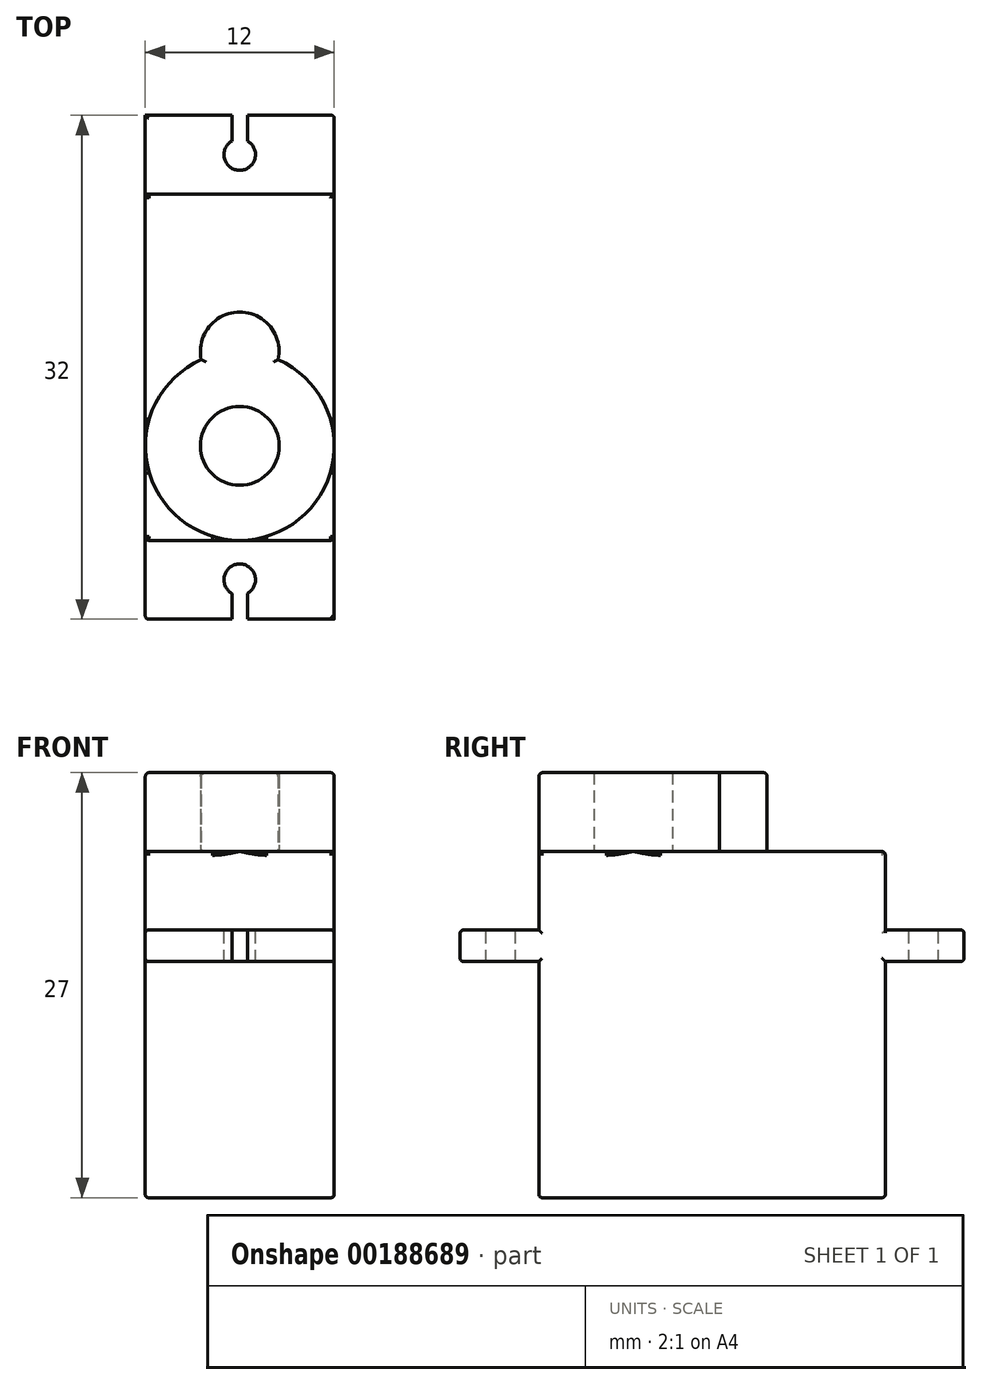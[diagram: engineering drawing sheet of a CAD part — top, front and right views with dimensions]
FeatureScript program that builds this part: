
annotation { "Feature Type Name" : "Feature", "Feature Type Description" : "" }
export const myFeature = defineFeature(function(context is Context, id is Id, definition is map)
    precondition{}
    {
        {
            var Q0;
            Q0=qCreatedBy(makeId("Top.planeOp"),FACE);
            var sketch = newSketch(context, id + "F0", { "sketchPlane" : qUnion([Q0])});
            skLineSegment(sketch, "E0.bottom", {"start": v(-8.25, -0.4) * mm, "end": v(3.75, -0.4) * mm});
            skLineSegment(sketch, "E0.top", {"start": v(-8.25, -22.4) * mm, "end": v(3.75, -22.4) * mm});
            skLineSegment(sketch, "E0.left", {"start": v(-8.25, -0.4) * mm, "end": v(-8.25, -22.4) * mm});
            skLineSegment(sketch, "E0.right", {"start": v(3.75, -0.4) * mm, "end": v(3.75, -22.4) * mm});
            skSolve(sketch);
        }
        {
            var Q0;
            Q0=makeQuery(id+"F0.imprint","IMPRINT",FACE,{"disambiguationData":[TD([[makeQuery(id+"F0.imprint","IMPRINT",EDGE,{"derivedFrom":sQuery(id+"F0.wireOp",EDGE,"E0.bottom")}),-1.0]])]});
            extrude(context, id + "F1", {"entities" : qUnion([Q0]), "depth" : 22 * mm});
        }
        {
            var Q0;
            Q0=makeQuery(id+"F1.opExtrude","CAP_FACE",FACE,{"disambiguationData":[OSD([sQuery(id+"F0.wireOp",EDGE,"E0.bottom"),sQuery(id+"F0.wireOp",EDGE,"E0.top"),sQuery(id+"F0.wireOp",EDGE,"E0.left"),sQuery(id+"F0.wireOp",EDGE,"E0.right")])],"isStart":false});
            var sketch = newSketch(context, id + "F2", { "sketchPlane" : qUnion([Q0])});
            skCircle(sketch, "E1", {"center": v(-2.25, -16.4) * mm, "radius": 6 * mm});
            skCircle(sketch, "E2", {"center": v(-2.25, -16.4) * mm, "radius": 2.5 * mm});
            skCircle(sketch, "E3", {"center": v(-2.25, -10.4) * mm, "radius": 2.5 * mm});
            skSolve(sketch);
        }
        {
            var Q0;
            {var subQ0=sQuery(id+"F2.wireOp",EDGE,"E3");var subQ1=sQuery(id+"F2.wireOp",EDGE,"E1");var subQ3=makeQuery(id+"F2.imprint","INTERSECT",VERTEX,{"disambiguationData":[OD(0.0)],"derivedFrom":[subQ1,subQ0]});Q0=makeQuery(id+"F2.imprint","IMPRINT",FACE,{"disambiguationData":[TD([[makeQuery(id+"F2.imprint","IMPRINT",EDGE,{"disambiguationData":[TD([[subQ3,-1.0]])],"derivedFrom":subQ1}),-1.0]])]});}
            var Q1;
            {var subQ0=sQuery(id+"F2.wireOp",EDGE,"E3");var subQ1=sQuery(id+"F2.wireOp",EDGE,"E1");var subQ3=makeQuery(id+"F2.imprint","INTERSECT",VERTEX,{"disambiguationData":[OD(0.0)],"derivedFrom":[subQ1,subQ0]});Q1=makeQuery(id+"F2.imprint","IMPRINT",FACE,{"disambiguationData":[TD([[makeQuery(id+"F2.imprint","IMPRINT",EDGE,{"disambiguationData":[TD([[subQ3,-1.0]])],"derivedFrom":subQ1}),1.0]])]});}
            var Q2;
            Q2=makeQuery(id+"F2.imprint","IMPRINT",FACE,{"disambiguationData":[TD([[makeQuery(id+"F2.imprint","IMPRINT",EDGE,{"derivedFrom":sQuery(id+"F2.wireOp",EDGE,"E2")}),-1.0]])]});
            extrude(context, id + "F3", {"entities" : qUnion([Q0, Q1, Q2]), "operationType" : NewBodyOperationType.ADD, "depth" : 5 * mm});
        }
        {
            var Q0;
            Q0=makeQuery(id+"F3.opExtrude","CAP_EDGE",EDGE,{"disambiguationData":[OSD([sQuery(id+"F2.wireOp",EDGE,"E1")])],"isStart":false});
            var Q1;
            Q1=makeQuery(id+"F3.opExtrude","CAP_EDGE",EDGE,{"disambiguationData":[OSD([sQuery(id+"F2.wireOp",EDGE,"E3")])],"isStart":false});
            var Q2;
            {var subQ0=sQuery(id+"F0.wireOp",EDGE,"E0.right");var subQ1=sQuery(id+"F0.wireOp",EDGE,"E0.bottom");Q2=makeQuery(id+"F3.boolean.opBoolean","SPLIT",EDGE,{"disambiguationData":[TD([makeQuery(id+"F1.opExtrude","SWEPT_FACE",FACE,{"disambiguationData":[OSD([subQ1])]})])],"derivedFrom":makeQuery(id+"F1.opExtrude","CAP_EDGE",EDGE,{"disambiguationData":[OSD([subQ0])],"isStart":false})});}
            var Q3;
            Q3=makeQuery(id+"F1.opExtrude","CAP_EDGE",EDGE,{"disambiguationData":[OSD([sQuery(id+"F0.wireOp",EDGE,"E0.bottom")])],"isStart":false});
            var Q4;
            {var subQ0=sQuery(id+"F0.wireOp",EDGE,"E0.left");var subQ1=sQuery(id+"F0.wireOp",EDGE,"E0.bottom");Q4=makeQuery(id+"F3.boolean.opBoolean","SPLIT",EDGE,{"disambiguationData":[TD([makeQuery(id+"F1.opExtrude","SWEPT_FACE",FACE,{"disambiguationData":[OSD([subQ1])]})])],"derivedFrom":makeQuery(id+"F1.opExtrude","CAP_EDGE",EDGE,{"disambiguationData":[OSD([subQ0])],"isStart":false})});}
            var Q5;
            {var subQ0=sQuery(id+"F0.wireOp",EDGE,"E0.right");var subQ1=sQuery(id+"F0.wireOp",EDGE,"E0.top");Q5=makeQuery(id+"F3.boolean.opBoolean","SPLIT",EDGE,{"disambiguationData":[TD([makeQuery(id+"F1.opExtrude","SWEPT_FACE",FACE,{"disambiguationData":[OSD([subQ1])]})])],"derivedFrom":makeQuery(id+"F1.opExtrude","CAP_EDGE",EDGE,{"disambiguationData":[OSD([subQ0])],"isStart":false})});}
            var Q6;
            {var subQ0=sQuery(id+"F0.wireOp",EDGE,"E0.top");var subQ1=sQuery(id+"F0.wireOp",EDGE,"E0.right");Q6=makeQuery(id+"F3.boolean.opBoolean","SPLIT",EDGE,{"disambiguationData":[TD([makeQuery(id+"F1.opExtrude","SWEPT_FACE",FACE,{"disambiguationData":[OSD([subQ1])]})])],"derivedFrom":makeQuery(id+"F1.opExtrude","CAP_EDGE",EDGE,{"disambiguationData":[OSD([subQ0])],"isStart":false})});}
            var Q7;
            {var subQ0=sQuery(id+"F0.wireOp",EDGE,"E0.top");var subQ1=sQuery(id+"F0.wireOp",EDGE,"E0.left");Q7=makeQuery(id+"F3.boolean.opBoolean","SPLIT",EDGE,{"disambiguationData":[TD([makeQuery(id+"F1.opExtrude","SWEPT_FACE",FACE,{"disambiguationData":[OSD([subQ1])]})])],"derivedFrom":makeQuery(id+"F1.opExtrude","CAP_EDGE",EDGE,{"disambiguationData":[OSD([subQ0])],"isStart":false})});}
            var Q8;
            {var subQ0=sQuery(id+"F0.wireOp",EDGE,"E0.left");var subQ1=sQuery(id+"F0.wireOp",EDGE,"E0.top");Q8=makeQuery(id+"F3.boolean.opBoolean","SPLIT",EDGE,{"disambiguationData":[TD([makeQuery(id+"F1.opExtrude","SWEPT_FACE",FACE,{"disambiguationData":[OSD([subQ1])]})])],"derivedFrom":makeQuery(id+"F1.opExtrude","CAP_EDGE",EDGE,{"disambiguationData":[OSD([subQ0])],"isStart":false})});}
            fillet(context, id + "F4", {"entities" : qUnion([Q0, Q1, Q2, Q3, Q4, Q5, Q6, Q7, Q8]), "radius" : .25 * mm, "tangentPropagation" : true, "allowEdgeOverflow" : false});
        }
        {
            var Q0;
            Q0=makeQuery(id+"F1.opExtrude","SWEPT_FACE",FACE,{"disambiguationData":[OSD([sQuery(id+"F0.wireOp",EDGE,"E0.bottom")])]});
            var sketch = newSketch(context, id + "F5", { "sketchPlane" : qUnion([Q0])});
            skLineSegment(sketch, "E4.bottom", {"start": v(-3.75, 17) * mm, "end": v(8.25, 17) * mm});
            skLineSegment(sketch, "E4.top", {"start": v(-3.75, 15) * mm, "end": v(8.25, 15) * mm});
            skLineSegment(sketch, "E4.left", {"start": v(-3.75, 17) * mm, "end": v(-3.75, 15) * mm});
            skLineSegment(sketch, "E4.right", {"start": v(8.25, 17) * mm, "end": v(8.25, 15) * mm});
            skSolve(sketch);
        }
        {
            var Q0;
            Q0=makeQuery(id+"F1.opExtrude","SWEPT_FACE",FACE,{"disambiguationData":[OSD([sQuery(id+"F0.wireOp",EDGE,"E0.top")])]});
            var sketch = newSketch(context, id + "F6", { "sketchPlane" : qUnion([Q0])});
            skLineSegment(sketch, "E5.bottom", {"start": v(-8.25, 17) * mm, "end": v(3.75, 17) * mm});
            skLineSegment(sketch, "E5.top", {"start": v(-8.25, 15) * mm, "end": v(3.75, 15) * mm});
            skLineSegment(sketch, "E5.left", {"start": v(-8.25, 17) * mm, "end": v(-8.25, 15) * mm});
            skLineSegment(sketch, "E5.right", {"start": v(3.75, 17) * mm, "end": v(3.75, 15) * mm});
            skSolve(sketch);
        }
        {
            var Q0;
            Q0=makeQuery(id+"F6.imprint","IMPRINT",FACE,{"disambiguationData":[TD([[makeQuery(id+"F6.imprint","IMPRINT",EDGE,{"derivedFrom":sQuery(id+"F6.wireOp",EDGE,"E5.bottom")}),-1.0]])]});
            extrude(context, id + "F7", {"entities" : qUnion([Q0]), "operationType" : NewBodyOperationType.ADD, "depth" : 5 * mm});
        }
        {
            var Q0;
            Q0=makeQuery(id+"F5.imprint","IMPRINT",FACE,{"disambiguationData":[TD([[makeQuery(id+"F5.imprint","IMPRINT",EDGE,{"derivedFrom":sQuery(id+"F5.wireOp",EDGE,"E4.bottom")}),-1.0]])]});
            extrude(context, id + "F8", {"entities" : qUnion([Q0]), "operationType" : NewBodyOperationType.ADD, "depth" : 5 * mm});
        }
        {
            var Q0;
            Q0=makeQuery(id+"F7.opExtrude","SWEPT_FACE",FACE,{"disambiguationData":[OSD([sQuery(id+"F6.wireOp",EDGE,"E5.bottom")])]});
            var sketch = newSketch(context, id + "F9", { "sketchPlane" : qUnion([Q0])});
            skCircle(sketch, "E6", {"center": v(-2.25, -24.9) * mm, "radius": 1 * mm});
            skLineSegment(sketch, "E7.bottom", {"start": v(-2.75, -25.77) * mm, "end": v(-1.75, -25.77) * mm});
            skLineSegment(sketch, "E7.top", {"start": v(-2.75, -27.4) * mm, "end": v(-1.75, -27.4) * mm});
            skLineSegment(sketch, "E7.left", {"start": v(-2.75, -25.77) * mm, "end": v(-2.75, -27.4) * mm});
            skLineSegment(sketch, "E7.right", {"start": v(-1.75, -25.77) * mm, "end": v(-1.75, -27.4) * mm});
            skSolve(sketch);
        }
        {
            var Q0;
            {var subQ0=sQuery(id+"F9.wireOp",EDGE,"E7.bottom");Q0=makeQuery(id+"F9.imprint","IMPRINT",FACE,{"disambiguationData":[TD([[makeQuery(id+"F9.imprint","IMPRINT",EDGE,{"derivedFrom":subQ0}),1.0]])]});}
            var Q1;
            Q1=makeQuery(id+"F9.imprint","IMPRINT",FACE,{"disambiguationData":[TD([[makeQuery(id+"F9.imprint","IMPRINT",EDGE,{"derivedFrom":sQuery(id+"F9.wireOp",EDGE,"E7.top")}),1.0]])]});
            var Q2;
            {var subQ0=sQuery(id+"F9.wireOp",EDGE,"E7.bottom");Q2=makeQuery(id+"F9.imprint","IMPRINT",FACE,{"disambiguationData":[TD([[makeQuery(id+"F9.imprint","IMPRINT",EDGE,{"derivedFrom":subQ0}),-1.0]])]});}
            extrude(context, id + "F10", {"entities" : qUnion([Q0, Q1, Q2]), "operationType" : NewBodyOperationType.REMOVE, "oppositeDirection" : true, "depth" : 2 * mm});
        }
        {
            var Q0;
            Q0=makeQuery(id+"F8.opExtrude","SWEPT_FACE",FACE,{"disambiguationData":[OSD([sQuery(id+"F5.wireOp",EDGE,"E4.bottom")])]});
            var sketch = newSketch(context, id + "F11", { "sketchPlane" : qUnion([Q0])});
            skCircle(sketch, "E8", {"center": v(-2.25, 2.1) * mm, "radius": 1 * mm});
            skLineSegment(sketch, "E9.bottom", {"start": v(-2.75, 4.6) * mm, "end": v(-1.75, 4.6) * mm});
            skLineSegment(sketch, "E9.top", {"start": v(-2.75, 2.6) * mm, "end": v(-1.75, 2.6) * mm});
            skLineSegment(sketch, "E9.left", {"start": v(-2.75, 4.6) * mm, "end": v(-2.75, 2.6) * mm});
            skLineSegment(sketch, "E9.right", {"start": v(-1.75, 4.6) * mm, "end": v(-1.75, 2.6) * mm});
            skSolve(sketch);
        }
        {
            var Q0;
            Q0=qSketchRegion(id+"F11",true);
            extrude(context, id + "F12", {"entities" : qUnion([Q0]), "operationType" : NewBodyOperationType.REMOVE, "oppositeDirection" : true, "depth" : 2 * mm});
        }
        {
            var Q0;
            Q0=makeQuery(id+"F8.opExtrude","SWEPT_EDGE",EDGE,{"disambiguationData":[OSD([sQuery(id+"F0.wireOp",EDGE,"E0.bottom"),sQuery(id+"F0.wireOp",EDGE,"E0.left"),sQuery(id+"F5.wireOp",EDGE,"E4.bottom"),sQuery(id+"F5.wireOp",EDGE,"E4.right")])]});
            var Q1;
            {var subQ0=sQuery(id+"F5.wireOp",EDGE,"E4.bottom");Q1=makeQuery(id+"F12.boolean.opBoolean","SPLIT",EDGE,{"disambiguationData":[TD([makeQuery(id+"F1.opExtrude","SWEPT_FACE",FACE,{"disambiguationData":[OSD([sQuery(id+"F0.wireOp",EDGE,"E0.left")])]})])],"derivedFrom":makeQuery(id+"F8.opExtrude","CAP_EDGE",EDGE,{"disambiguationData":[OSD([subQ0])],"isStart":false})});}
            var Q2;
            Q2=makeQuery(id+"F12.boolean.opBoolean","COPY",EDGE,{"derivedFrom":makeQuery(id+"F12.opExtrude","CAP_EDGE",EDGE,{"disambiguationData":[OSD([sQuery(id+"F11.wireOp",EDGE,"E9.left")])],"isStart":true})});
            var Q3;
            Q3=makeQuery(id+"F12.boolean.opBoolean","COPY",EDGE,{"derivedFrom":makeQuery(id+"F12.opExtrude","CAP_EDGE",EDGE,{"disambiguationData":[OSD([sQuery(id+"F11.wireOp",EDGE,"E8")])],"isStart":true})});
            var Q4;
            Q4=makeQuery(id+"F12.boolean.opBoolean","COPY",EDGE,{"derivedFrom":makeQuery(id+"F12.opExtrude","CAP_EDGE",EDGE,{"disambiguationData":[OSD([sQuery(id+"F11.wireOp",EDGE,"E9.right")])],"isStart":true})});
            var Q5;
            {var subQ0=sQuery(id+"F5.wireOp",EDGE,"E4.bottom");Q5=makeQuery(id+"F12.boolean.opBoolean","SPLIT",EDGE,{"disambiguationData":[TD([makeQuery(id+"F1.opExtrude","SWEPT_FACE",FACE,{"disambiguationData":[OSD([sQuery(id+"F0.wireOp",EDGE,"E0.right")])]})])],"derivedFrom":makeQuery(id+"F8.opExtrude","CAP_EDGE",EDGE,{"disambiguationData":[OSD([subQ0])],"isStart":false})});}
            var Q6;
            Q6=makeQuery(id+"F8.opExtrude","SWEPT_EDGE",EDGE,{"disambiguationData":[OSD([sQuery(id+"F0.wireOp",EDGE,"E0.bottom"),sQuery(id+"F0.wireOp",EDGE,"E0.right"),sQuery(id+"F5.wireOp",EDGE,"E4.bottom"),sQuery(id+"F5.wireOp",EDGE,"E4.left")])]});
            var Q7;
            Q7=makeQuery(id+"F7.opExtrude","SWEPT_EDGE",EDGE,{"disambiguationData":[OSD([sQuery(id+"F0.wireOp",EDGE,"E0.top"),sQuery(id+"F0.wireOp",EDGE,"E0.right"),sQuery(id+"F6.wireOp",EDGE,"E5.bottom"),sQuery(id+"F6.wireOp",EDGE,"E5.right")])]});
            var Q8;
            {var subQ0=sQuery(id+"F6.wireOp",EDGE,"E5.bottom");Q8=makeQuery(id+"F10.boolean.opBoolean","SPLIT",EDGE,{"disambiguationData":[TD([makeQuery(id+"F1.opExtrude","SWEPT_FACE",FACE,{"disambiguationData":[OSD([sQuery(id+"F0.wireOp",EDGE,"E0.right")])]})])],"derivedFrom":makeQuery(id+"F7.opExtrude","CAP_EDGE",EDGE,{"disambiguationData":[OSD([subQ0])],"isStart":false})});}
            var Q9;
            {var subQ0=sQuery(id+"F6.wireOp",EDGE,"E5.top");Q9=makeQuery(id+"F10.boolean.opBoolean","SPLIT",EDGE,{"disambiguationData":[TD([makeQuery(id+"F1.opExtrude","SWEPT_FACE",FACE,{"disambiguationData":[OSD([sQuery(id+"F0.wireOp",EDGE,"E0.right")])]})])],"derivedFrom":makeQuery(id+"F7.opExtrude","CAP_EDGE",EDGE,{"disambiguationData":[OSD([subQ0])],"isStart":false})});}
            var Q10;
            Q10=makeQuery(id+"F7.opExtrude","SWEPT_EDGE",EDGE,{"disambiguationData":[OSD([sQuery(id+"F0.wireOp",EDGE,"E0.top"),sQuery(id+"F0.wireOp",EDGE,"E0.right"),sQuery(id+"F6.wireOp",EDGE,"E5.top"),sQuery(id+"F6.wireOp",EDGE,"E5.right")])]});
            var Q11;
            Q11=makeQuery(id+"F10.boolean.opBoolean","COPY",EDGE,{"derivedFrom":makeQuery(id+"F10.opExtrude","SWEPT_EDGE",EDGE,{"disambiguationData":[OSD([sQuery(id+"F6.wireOp",EDGE,"E5.bottom"),sQuery(id+"F9.wireOp",EDGE,"E7.top"),sQuery(id+"F9.wireOp",EDGE,"E7.right")])]})});
            var Q12;
            Q12=makeQuery(id+"F10.boolean.opBoolean","COPY",EDGE,{"derivedFrom":makeQuery(id+"F10.opExtrude","SWEPT_EDGE",EDGE,{"disambiguationData":[OSD([sQuery(id+"F6.wireOp",EDGE,"E5.bottom"),sQuery(id+"F9.wireOp",EDGE,"E7.top"),sQuery(id+"F9.wireOp",EDGE,"E7.left")])]})});
            var Q13;
            Q13=makeQuery(id+"F10.boolean.opBoolean","COPY",EDGE,{"derivedFrom":makeQuery(id+"F10.opExtrude","CAP_EDGE",EDGE,{"disambiguationData":[OSD([sQuery(id+"F9.wireOp",EDGE,"E7.left")])],"isStart":true})});
            var Q14;
            Q14=makeQuery(id+"F10.boolean.opBoolean","COPY",EDGE,{"derivedFrom":makeQuery(id+"F10.opExtrude","CAP_EDGE",EDGE,{"disambiguationData":[OSD([sQuery(id+"F9.wireOp",EDGE,"E6")])],"isStart":true})});
            var Q15;
            Q15=makeQuery(id+"F10.boolean.opBoolean","COPY",EDGE,{"derivedFrom":makeQuery(id+"F10.opExtrude","CAP_EDGE",EDGE,{"disambiguationData":[OSD([sQuery(id+"F9.wireOp",EDGE,"E7.left")])],"isStart":false})});
            var Q16;
            Q16=makeQuery(id+"F10.boolean.opBoolean","COPY",EDGE,{"derivedFrom":makeQuery(id+"F10.opExtrude","CAP_EDGE",EDGE,{"disambiguationData":[OSD([sQuery(id+"F9.wireOp",EDGE,"E6")])],"isStart":false})});
            var Q17;
            {var subQ0=sQuery(id+"F6.wireOp",EDGE,"E5.top");Q17=makeQuery(id+"F10.boolean.opBoolean","SPLIT",EDGE,{"disambiguationData":[TD([makeQuery(id+"F1.opExtrude","SWEPT_FACE",FACE,{"disambiguationData":[OSD([sQuery(id+"F0.wireOp",EDGE,"E0.left")])]})])],"derivedFrom":makeQuery(id+"F7.opExtrude","CAP_EDGE",EDGE,{"disambiguationData":[OSD([subQ0])],"isStart":false})});}
            var Q18;
            {var subQ0=sQuery(id+"F6.wireOp",EDGE,"E5.bottom");Q18=makeQuery(id+"F10.boolean.opBoolean","SPLIT",EDGE,{"disambiguationData":[TD([makeQuery(id+"F1.opExtrude","SWEPT_FACE",FACE,{"disambiguationData":[OSD([sQuery(id+"F0.wireOp",EDGE,"E0.left")])]})])],"derivedFrom":makeQuery(id+"F7.opExtrude","CAP_EDGE",EDGE,{"disambiguationData":[OSD([subQ0])],"isStart":false})});}
            var Q19;
            Q19=makeQuery(id+"F7.opExtrude","CAP_EDGE",EDGE,{"disambiguationData":[OSD([sQuery(id+"F6.wireOp",EDGE,"E5.left")])],"isStart":false});
            var Q20;
            {var subQ0=sQuery(id+"F0.wireOp",EDGE,"E0.top");var subQ1=sQuery(id+"F0.wireOp",EDGE,"E0.right");Q20=makeQuery(id+"F7.boolean.opBoolean","SPLIT",EDGE,{"disambiguationData":[TD([makeQuery(id+"F7.opExtrude","SWEPT_FACE",FACE,{"disambiguationData":[OSD([sQuery(id+"F6.wireOp",EDGE,"E5.top")])]})])],"derivedFrom":makeQuery(id+"F1.opExtrude","SWEPT_EDGE",EDGE,{"disambiguationData":[OSD([subQ0,subQ1])]})});}
            var Q21;
            {var subQ0=sQuery(id+"F0.wireOp",EDGE,"E0.top");var subQ1=sQuery(id+"F0.wireOp",EDGE,"E0.right");Q21=makeQuery(id+"F7.boolean.opBoolean","SPLIT",EDGE,{"disambiguationData":[TD([makeQuery(id+"F7.opExtrude","SWEPT_FACE",FACE,{"disambiguationData":[OSD([sQuery(id+"F6.wireOp",EDGE,"E5.bottom")])]})])],"derivedFrom":makeQuery(id+"F1.opExtrude","SWEPT_EDGE",EDGE,{"disambiguationData":[OSD([subQ0,subQ1])]})});}
            var Q22;
            {var subQ0=sQuery(id+"F0.wireOp",EDGE,"E0.top");var subQ1=sQuery(id+"F0.wireOp",EDGE,"E0.left");Q22=makeQuery(id+"F7.boolean.opBoolean","SPLIT",EDGE,{"disambiguationData":[TD([makeQuery(id+"F7.opExtrude","SWEPT_FACE",FACE,{"disambiguationData":[OSD([sQuery(id+"F6.wireOp",EDGE,"E5.bottom")])]})])],"derivedFrom":makeQuery(id+"F1.opExtrude","SWEPT_EDGE",EDGE,{"disambiguationData":[OSD([subQ0,subQ1])]})});}
            var Q23;
            Q23=makeQuery(id+"F10.boolean.opBoolean","COPY",EDGE,{"derivedFrom":makeQuery(id+"F10.opExtrude","CAP_EDGE",EDGE,{"disambiguationData":[OSD([sQuery(id+"F9.wireOp",EDGE,"E7.right")])],"isStart":false})});
            var Q24;
            Q24=makeQuery(id+"F7.opExtrude","SWEPT_EDGE",EDGE,{"disambiguationData":[OSD([sQuery(id+"F0.wireOp",EDGE,"E0.top"),sQuery(id+"F0.wireOp",EDGE,"E0.left"),sQuery(id+"F6.wireOp",EDGE,"E5.top"),sQuery(id+"F6.wireOp",EDGE,"E5.left")])]});
            var Q25;
            Q25=makeQuery(id+"F7.opExtrude","SWEPT_EDGE",EDGE,{"disambiguationData":[OSD([sQuery(id+"F0.wireOp",EDGE,"E0.top"),sQuery(id+"F0.wireOp",EDGE,"E0.left"),sQuery(id+"F6.wireOp",EDGE,"E5.bottom"),sQuery(id+"F6.wireOp",EDGE,"E5.left")])]});
            var Q26;
            {var subQ0=sQuery(id+"F0.wireOp",EDGE,"E0.top");var subQ1=sQuery(id+"F0.wireOp",EDGE,"E0.left");Q26=makeQuery(id+"F7.boolean.opBoolean","SPLIT",EDGE,{"disambiguationData":[TD([makeQuery(id+"F7.opExtrude","SWEPT_FACE",FACE,{"disambiguationData":[OSD([sQuery(id+"F6.wireOp",EDGE,"E5.top")])]})])],"derivedFrom":makeQuery(id+"F1.opExtrude","SWEPT_EDGE",EDGE,{"disambiguationData":[OSD([subQ0,subQ1])]})});}
            var Q27;
            Q27=makeQuery(id+"F1.opExtrude","CAP_EDGE",EDGE,{"disambiguationData":[OSD([sQuery(id+"F0.wireOp",EDGE,"E0.left")])],"isStart":true});
            var Q28;
            Q28=makeQuery(id+"F1.opExtrude","CAP_EDGE",EDGE,{"disambiguationData":[OSD([sQuery(id+"F0.wireOp",EDGE,"E0.top")])],"isStart":true});
            var Q29;
            {var subQ0=sQuery(id+"F0.wireOp",EDGE,"E0.bottom");var subQ1=sQuery(id+"F0.wireOp",EDGE,"E0.left");Q29=makeQuery(id+"F8.boolean.opBoolean","SPLIT",EDGE,{"disambiguationData":[TD([makeQuery(id+"F8.opExtrude","SWEPT_FACE",FACE,{"disambiguationData":[OSD([sQuery(id+"F5.wireOp",EDGE,"E4.top")])]})])],"derivedFrom":makeQuery(id+"F1.opExtrude","SWEPT_EDGE",EDGE,{"disambiguationData":[OSD([subQ0,subQ1])]})});}
            var Q30;
            Q30=makeQuery(id+"F8.opExtrude","SWEPT_EDGE",EDGE,{"disambiguationData":[OSD([sQuery(id+"F0.wireOp",EDGE,"E0.bottom"),sQuery(id+"F0.wireOp",EDGE,"E0.left"),sQuery(id+"F5.wireOp",EDGE,"E4.top"),sQuery(id+"F5.wireOp",EDGE,"E4.right")])]});
            var Q31;
            {var subQ0=sQuery(id+"F5.wireOp",EDGE,"E4.top");Q31=makeQuery(id+"F12.boolean.opBoolean","SPLIT",EDGE,{"disambiguationData":[TD([makeQuery(id+"F1.opExtrude","SWEPT_FACE",FACE,{"disambiguationData":[OSD([sQuery(id+"F0.wireOp",EDGE,"E0.left")])]})])],"derivedFrom":makeQuery(id+"F8.opExtrude","CAP_EDGE",EDGE,{"disambiguationData":[OSD([subQ0])],"isStart":false})});}
            var Q32;
            Q32=makeQuery(id+"F12.boolean.opBoolean","COPY",EDGE,{"derivedFrom":makeQuery(id+"F12.opExtrude","CAP_EDGE",EDGE,{"disambiguationData":[OSD([sQuery(id+"F11.wireOp",EDGE,"E8")])],"isStart":false})});
            var Q33;
            Q33=makeQuery(id+"F12.boolean.opBoolean","COPY",EDGE,{"derivedFrom":makeQuery(id+"F12.opExtrude","CAP_EDGE",EDGE,{"disambiguationData":[OSD([sQuery(id+"F11.wireOp",EDGE,"E9.left")])],"isStart":false})});
            var Q34;
            Q34=makeQuery(id+"F12.boolean.opBoolean","COPY",EDGE,{"derivedFrom":makeQuery(id+"F12.opExtrude","CAP_EDGE",EDGE,{"disambiguationData":[OSD([sQuery(id+"F11.wireOp",EDGE,"E9.right")])],"isStart":false})});
            var Q35;
            {var subQ0=sQuery(id+"F0.wireOp",EDGE,"E0.bottom");var subQ1=sQuery(id+"F0.wireOp",EDGE,"E0.left");Q35=makeQuery(id+"F8.boolean.opBoolean","SPLIT",EDGE,{"disambiguationData":[TD([makeQuery(id+"F4.opFillet","BLEND_FACE",FACE,{"disambiguationData":[OSD([subQ0])]})])],"derivedFrom":makeQuery(id+"F1.opExtrude","SWEPT_EDGE",EDGE,{"disambiguationData":[OSD([subQ0,subQ1])]})});}
            var Q36;
            {var subQ0=sQuery(id+"F0.wireOp",EDGE,"E0.bottom");var subQ1=sQuery(id+"F0.wireOp",EDGE,"E0.right");Q36=makeQuery(id+"F8.boolean.opBoolean","SPLIT",EDGE,{"disambiguationData":[TD([makeQuery(id+"F8.opExtrude","SWEPT_FACE",FACE,{"disambiguationData":[OSD([sQuery(id+"F5.wireOp",EDGE,"E4.top")])]})])],"derivedFrom":makeQuery(id+"F1.opExtrude","SWEPT_EDGE",EDGE,{"disambiguationData":[OSD([subQ0,subQ1])]})});}
            var Q37;
            Q37=makeQuery(id+"F1.opExtrude","CAP_EDGE",EDGE,{"disambiguationData":[OSD([sQuery(id+"F0.wireOp",EDGE,"E0.right")])],"isStart":true});
            var Q38;
            Q38=makeQuery(id+"F1.opExtrude","CAP_EDGE",EDGE,{"disambiguationData":[OSD([sQuery(id+"F0.wireOp",EDGE,"E0.bottom")])],"isStart":true});
            var Q39;
            Q39=makeQuery(id+"F8.opExtrude","SWEPT_EDGE",EDGE,{"disambiguationData":[OSD([sQuery(id+"F0.wireOp",EDGE,"E0.bottom"),sQuery(id+"F0.wireOp",EDGE,"E0.right"),sQuery(id+"F5.wireOp",EDGE,"E4.top"),sQuery(id+"F5.wireOp",EDGE,"E4.left")])]});
            var Q40;
            Q40=makeQuery(id+"F8.opExtrude","CAP_EDGE",EDGE,{"disambiguationData":[OSD([sQuery(id+"F5.wireOp",EDGE,"E4.left")])],"isStart":false});
            var Q41;
            {var subQ0=sQuery(id+"F5.wireOp",EDGE,"E4.top");Q41=makeQuery(id+"F12.boolean.opBoolean","SPLIT",EDGE,{"disambiguationData":[TD([makeQuery(id+"F1.opExtrude","SWEPT_FACE",FACE,{"disambiguationData":[OSD([sQuery(id+"F0.wireOp",EDGE,"E0.right")])]})])],"derivedFrom":makeQuery(id+"F8.opExtrude","CAP_EDGE",EDGE,{"disambiguationData":[OSD([subQ0])],"isStart":false})});}
            fillet(context, id + "F13", {"entities" : qUnion([Q0, Q1, Q2, Q3, Q4, Q5, Q6, Q7, Q8, Q9, Q10, Q11, Q12, Q13, Q14, Q15, Q16, Q17, Q18, Q19, Q20, Q21, Q22, Q23, Q24, Q25, Q26, Q27, Q28, Q29, Q30, Q31, Q32, Q33, Q34, Q35, Q36, Q37, Q38, Q39, Q40, Q41]), "radius" : .2 * mm, "tangentPropagation" : true, "allowEdgeOverflow" : false});
        }
    });
